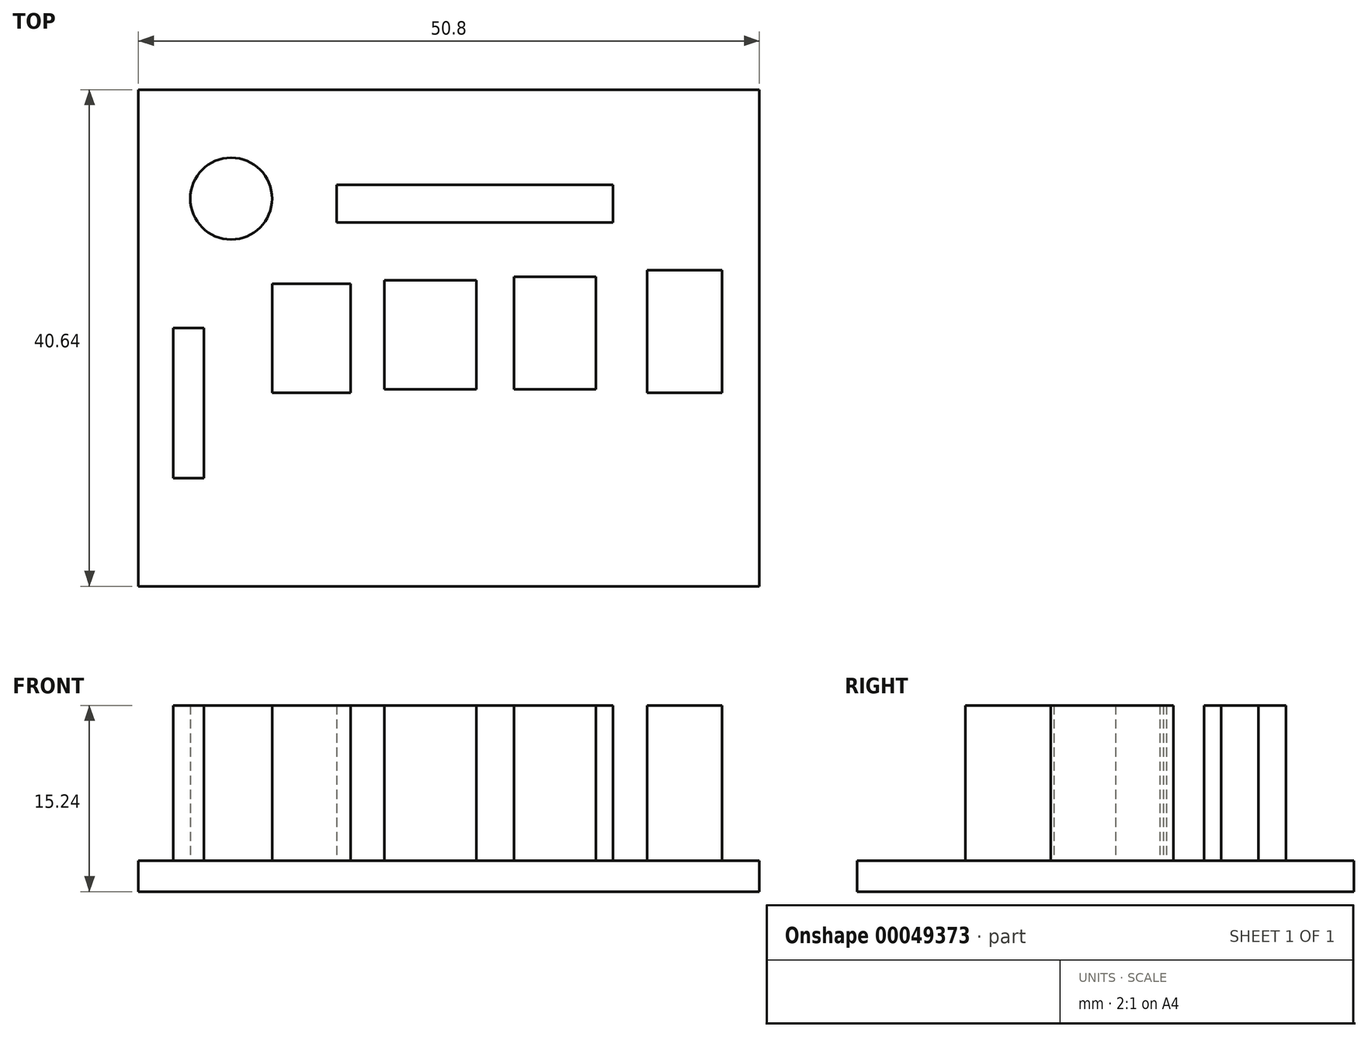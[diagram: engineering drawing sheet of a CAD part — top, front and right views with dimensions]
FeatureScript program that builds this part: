
annotation { "Feature Type Name" : "Feature", "Feature Type Description" : "" }
export const myFeature = defineFeature(function(context is Context, id is Id, definition is map)
    precondition{}
    {
        {
            var Q0;
            Q0=qCreatedBy(makeId("Top.planeOp"),FACE);
            var sketch = newSketch(context, id + "F0", { "sketchPlane" : qUnion([Q0])});
            skLineSegment(sketch, "E0.bottom", {"start": v(0, 0) * mm, "end": v(-50.8, 0) * mm});
            skLineSegment(sketch, "E0.top", {"start": v(0, -40.64) * mm, "end": v(-50.8, -40.64) * mm});
            skLineSegment(sketch, "E0.left", {"start": v(0, 0) * mm, "end": v(0, -40.64) * mm});
            skLineSegment(sketch, "E0.right", {"start": v(-50.8, 0) * mm, "end": v(-50.8, -40.64) * mm});
            skSolve(sketch);
        }
        {
            var Q0;
            Q0 = qSketchRegion(id + "F0", true);
            extrude(context, id + "F1", {"entities" : qUnion([Q0]), "depth" : 2.54 * mm});
        }
        {
            var Q0;
            Q0=makeQuery(id+"F1.opExtrude","CAP_FACE",FACE,{"disambiguationData":[OSD([sQuery(id+"F0.wireOp",EDGE,"E0.bottom"),sQuery(id+"F0.wireOp",EDGE,"E0.top"),sQuery(id+"F0.wireOp",EDGE,"E0.left"),sQuery(id+"F0.wireOp",EDGE,"E0.right")])],"isStart":false});
            var sketch = newSketch(context, id + "F2", { "sketchPlane" : qUnion([Q0])});
            skLineSegment(sketch, "E1.bottom", {"start": v(-39.87, -15.9) * mm, "end": v(-33.45, -15.9) * mm});
            skLineSegment(sketch, "E1.top", {"start": v(-39.87, -24.81) * mm, "end": v(-33.45, -24.81) * mm});
            skLineSegment(sketch, "E1.left", {"start": v(-39.87, -15.9) * mm, "end": v(-39.87, -24.81) * mm});
            skLineSegment(sketch, "E1.right", {"start": v(-33.45, -15.9) * mm, "end": v(-33.45, -24.81) * mm});
            skLineSegment(sketch, "E2.bottom", {"start": v(-30.67, -15.61) * mm, "end": v(-23.14, -15.61) * mm});
            skLineSegment(sketch, "E2.top", {"start": v(-30.67, -24.53) * mm, "end": v(-23.14, -24.53) * mm});
            skLineSegment(sketch, "E2.left", {"start": v(-30.67, -15.61) * mm, "end": v(-30.67, -24.53) * mm});
            skLineSegment(sketch, "E2.right", {"start": v(-23.14, -15.61) * mm, "end": v(-23.14, -24.53) * mm});
            skLineSegment(sketch, "E3.bottom", {"start": v(-20.07, -15.33) * mm, "end": v(-13.38, -15.33) * mm});
            skLineSegment(sketch, "E3.top", {"start": v(-20.07, -24.53) * mm, "end": v(-13.38, -24.53) * mm});
            skLineSegment(sketch, "E3.left", {"start": v(-20.07, -15.33) * mm, "end": v(-20.07, -24.53) * mm});
            skLineSegment(sketch, "E3.right", {"start": v(-13.38, -15.33) * mm, "end": v(-13.38, -24.53) * mm});
            skLineSegment(sketch, "E4.bottom", {"start": v(-9.2, -14.78) * mm, "end": v(-3.07, -14.78) * mm});
            skLineSegment(sketch, "E4.top", {"start": v(-9.2, -24.81) * mm, "end": v(-3.07, -24.81) * mm});
            skLineSegment(sketch, "E4.left", {"start": v(-9.2, -14.78) * mm, "end": v(-9.2, -24.81) * mm});
            skLineSegment(sketch, "E4.right", {"start": v(-3.07, -14.78) * mm, "end": v(-3.07, -24.81) * mm});
            skLineSegment(sketch, "E5.bottom", {"start": v(-34.57, -7.8) * mm, "end": v(-11.99, -7.8) * mm});
            skLineSegment(sketch, "E5.top", {"start": v(-34.57, -10.87) * mm, "end": v(-11.99, -10.87) * mm});
            skLineSegment(sketch, "E5.left", {"start": v(-34.57, -7.8) * mm, "end": v(-34.57, -10.87) * mm});
            skLineSegment(sketch, "E5.right", {"start": v(-11.99, -7.8) * mm, "end": v(-11.99, -10.87) * mm});
            skLineSegment(sketch, "E6.bottom", {"start": v(-47.95, -19.51) * mm, "end": v(-45.44, -19.51) * mm});
            skLineSegment(sketch, "E6.top", {"start": v(-47.95, -31.78) * mm, "end": v(-45.44, -31.78) * mm});
            skLineSegment(sketch, "E6.left", {"start": v(-47.95, -19.51) * mm, "end": v(-47.95, -31.78) * mm});
            skLineSegment(sketch, "E6.right", {"start": v(-45.44, -19.51) * mm, "end": v(-45.44, -31.78) * mm});
            skCircle(sketch, "E7", {"center": v(-43.21, -8.92) * mm, "radius": 3.35 * mm});
            skSolve(sketch);
        }
        {
            var Q0;
            Q0 = qSketchRegion(id + "F2", true);
            extrude(context, id + "F3", {"entities" : qUnion([Q0]), "operationType" : NewBodyOperationType.ADD, "depth" : 12.7 * mm});
        }
    });
